# Revit family: ElectricalFixture_WiringAccessories_Hager_Sollysta_RaisedPlateShaverSocket
name_source: partatom
category: Electrical Fixtures
revit_build: Autodesk Revit 2015 (Build: 20160512_1515(x64)
units: mm (PartAtom-declared; Revit-internal decimal feet)

## types (7) — shared parameters
CE Approval = Yes
Default Elevation = 1219.2 mm  [stored 4 ft]
Design Country = China
Distance From Centre = 22.4 mm
Distance From Edge = 63.6 mm
Expected Life = 25 years
Extrusion From Wall = 12.6 mm
Frequency = 50/60Hz
Gross Weight kg = 0.165
LED Indicator Switch = Yes
Manufacturer = Hager
Manufacturer Country = United Kingdom
Manufacturer Website = http://www.hager.co.uk
Overall Depth = 21.1 mm
Overall Height = 146 mm  [stored 0.479003 ft]
Overall Length = 65 mm  [stored 0.213255 ft]
Overall Width = 86 mm
Packaging Recyclable = Yes
Product Family = DecorativeShaverSocket_115/230VShaverSocket
Product Group = WiringAccessories
Product Literature = http://www.hager.co.uk
Product Range = Sollysta
Product URL = http://www.hager.co.uk
Reference Standard = BS 1363-2
Shape = Rectangular
Shipping Weight kg = 0.188
Supply Phase = 1
Switch = Yes
Type = ElectricalFixture
Voltage (Volts) = 230V/240V

## per-type parameters (varying)
| type | Colour | Description | EAN Code | Features | Finish | Insert Material | Material | Name | Technical Description |
| WRSO100PSW | PolishedSteel | 115/230VShaverOutletPolishedSteelWhiteInsert | 5015654744458 | 115/230VShaverOutletPolishedSteelWhiteInsert | Polished | Hager_WhiteInsert | Hager_PolishedSteel | DecorativeShaverSocket_WRSO100PSW | 115/230VShaverOutletPolishedSteelWhiteInsert |
| WRSO100BSW | BrushedSteel | 115/230VShaverOutletBrushedSteelWhiteInsert | 5015654744496 | 115/230VShaverOutletBrushedSteelWhiteInsert | Brushed | Hager_WhiteInsert | Hager_BrushedSteel | DecorativeShaverSocket_WRSO100BSW | 115/230VShaverOutletBrushedSteelWhiteInsert |
| WRSO100PBW | PolishedBrass | 115/230VShaverOutletPolishedBrassWhiteInsert | 5015654744533 | 115/230VShaverOutletPolishedBrassWhiteInsert | Polished | Hager_WhiteInsert | Hager_PolishedBrass | DecorativeShaverSocket_WRSO100PBW | 115/230VShaverOutletPolishedBrassWhiteInsert |
| WRSO100BNB | BlackNickel | 115/230VShaverOutletBlackNickelBlackInsert | 5015654744571 | 115/230VShaverOutletBlackNickelBlackInsert | BlackNickel | Hager_BlackInsert | Hager_BlackNickel | DecorativeShaverSocket_WRSO100PBW | 115/230VShaverOutletBlackNickelBlackInsert |
| WRSO100BSB | BrushedSteel | 115/230VShaverOutletBrushedSteelBlackInsert | 5015654744519 | 115/230VShaverOutletBrushedSteelBlackInsert | Brushed | Hager_BlackInsert | Hager_BrushedSteel | DecorativeShaverSocket_WRSO100BSB | 115/230VShaverOutletBrushedSteelBlackInsert |
| WRSO100PBB | PolishedBrass | 115/230VShaverOutletPolishedBrassBlackInsert | 5015654744557 | 115/230VShaverOutletPolishedBrassBlackInsert | Polished | Hager_BlackInsert | Hager_PolishedBrass | DecorativeShaverSocket_WRSO100PBB | 115/230VShaverOutletPolishedBrassBlackInsert |
| WRSO100PSB | PolishedSteel | 115/230VShaverOutletPolishedSteelBlackInsert | 5015654744472 | 115/230VShaverOutletPolishedSteelBlackInsert | Polished | Hager_WhiteInsert | Hager_PolishedSteel | DecorativeShaverSocket_WRSO100PSB | 115/230VShaverOutletPolishedSteelBlackInsert |

note: column(s) folded — value = type name in every type: Product Model Number, Unique Reference

note: [stored X ft] marks values corroborated as IEEE doubles in the binary element streams (Revit-internal decimal feet)

## geometry (parser evidence)
native form markers: Blend x2, Sweep x4
no freeform markers — native parametric forms only
